# Revit family: 4C-Max_Height_Units_FL.rfa
name_source: partatom
category: Specialty Equipment
revit_build: Autodesk Revit 2016 (Build: 20150714_1515(x64)
units: mm (PartAtom-declared; Revit-internal decimal feet)

## family parameters
Always vertical = Yes
Cut with Voids When Loaded = No
Host = Wall
Part Type = Normal
Room Calculation Point = No
Round Connector Dimension = Use Diameter
Shared = No

## types (12) — shared parameters
Assembly Code = C1030910
Back Enclosure Material = Aluminum - Salsbury Finish = Anodized
Depth = 17.025"
Height = 56.719"
Latch Locks Left Side = No
Latch Locks Right Side = No
Lock Material = Stainless Steel -Salsbury Finish =  Polished
Manufacturer = Salsbury Industries
MasterFormat Number = 10 55 00
MasterFormat Title = Postal Specialties
Version = 2.0 (08/09/16)

## per-type parameters (varying)
- 3716D-20 FL: Bottom Back Plate=Yes; Description=Max Height Unit: 20 MB1, 2 PL4.5, OM2; Door Slot L1=3700 Series 4C Door Configurations : MB1 Door; Door Slot L10=3700 Series 4C Door Configurations : MB1 Door w/ Divider; Door Slot L11=3700 Series 4C Door Configurations : MB1 Door w/ Divider; Door Slot L16=3700 Series 4C Parcel Configurations : PL4.5 w/ Divider; Door Slot L2=3700 Series 4C Door Configurations : MB1 Door w/ Divider; Door Slot L3=3700 Series 4C Door Configurations : MB1 Door w/ Divider; Door Slot L4=3700 Series 4C Door Configurations : MB1 Door w/ Divider; Door Slot L5=3700 Series 4C Door Configurations : MB1 Door w/ Divider; Door Slot L6=3700 Series 4C Door Configurations : MB1 Door w/ Divider; Door Slot L7=3700 Series 4C Door Configurations : MB1 Door w/ Divider; Door Slot L8=3700 Series 4C Door Configurations : MB1 Door w/ Divider; Door Slot L9=3700 Series 4C Door Configurations : MB1 Door w/ Divider; Door Slot R1=3700 Series 4C Door Configurations : MB1 Door; Door Slot R10=3700 Series 4C Door Configurations : MB1 Door w/ Divider; Door Slot R11=3700 Series 4C Door Configurations : MB1 Door w/ Divider; Door Slot R16=3700 Series 4C Parcel Configurations : PL4.5 w/ Divider; Door Slot R2=3700 Series 4C Door Configurations : MB1 Door w/ Divider; Door Slot R3=3700 Series 4C Door Configurations : MB1 Door w/ Divider; Door Slot R4=3700 Series 4C Door Configurations : MB1 Door w/ Divider; Door Slot R5=3700 Series 4C Door Configurations : MB1 Door w/ Divider; Door Slot R6=3700 Series 4C Door Configurations : MB1 Door w/ Divider; Door Slot R7=3700 Series 4C Door Configurations : Empty; Door Slot R8=3700 Series 4C OM2 Configuration : OM2-FL; Door Slot R9=3700 Series 4C Door Configurations : MB1 Door w/ Divider; Latch Alignment=14.857"; Left Inside Wall=Yes; Right Inside Wall=Yes; Top Back Plate=Yes; Type Comments=4C Standard Horizontal Mailbox - Front Loading; Vertical Center Divider=Yes; Width=31.098"
- 3716S-09 FL: Bottom Back Plate=No; Description=Max Height Unit: 9 MB1, 1 PL4.5, OM2; Door Slot L1=3700 Series 4C Door Configurations : Empty; Door Slot L10=3700 Series 4C Door Configurations : Empty; Door Slot L11=3700 Series 4C Door Configurations : Empty; Door Slot L16=3700 Series 4C Door Configurations : Empty; Door Slot L2=3700 Series 4C Door Configurations : Empty; Door Slot L3=3700 Series 4C Door Configurations : Empty; Door Slot L4=3700 Series 4C Door Configurations : Empty; Door Slot L5=3700 Series 4C Door Configurations : Empty; Door Slot L6=3700 Series 4C Door Configurations : Empty; Door Slot L7=3700 Series 4C Door Configurations : Empty; Door Slot L8=3700 Series 4C Door Configurations : Empty; Door Slot L9=3700 Series 4C Door Configurations : Empty; Door Slot R1=3700 Series 4C Door Configurations : MB1 Door; Door Slot R10=3700 Series 4C Door Configurations : MB1 Door w/ Divider; Door Slot R11=3700 Series 4C Door Configurations : MB1 Door w/ Divider; Door Slot R16=3700 Series 4C Parcel Configurations : PL4.5 w/ Divider; Door Slot R2=3700 Series 4C Door Configurations : MB1 Door w/ Divider; Door Slot R3=3700 Series 4C Door Configurations : MB1 Door w/ Divider; Door Slot R4=3700 Series 4C Door Configurations : MB1 Door w/ Divider; Door Slot R5=3700 Series 4C Door Configurations : MB1 Door w/ Divider; Door Slot R6=3700 Series 4C Door Configurations : MB1 Door w/ Divider; Door Slot R7=3700 Series 4C Door Configurations : Empty; Door Slot R8=3700 Series 4C OM2 Configuration : OM2-FL; Door Slot R9=3700 Series 4C Door Configurations : MB1 Door w/ Divider; Latch Alignment=13.876"; Left Inside Wall=No; Right Inside Wall=No; Top Back Plate=No; Type Comments=4C Standard Horizontal Mailbox - Front Loading; Vertical Center Divider=No; Width=16.344"
- 3716S-04 FL: Bottom Back Plate=No; Description=Max Height Unit: 3 MB2, 1 MB3, 1 PL4.5, OM2; Door Slot L1=3700 Series 4C Door Configurations : Empty; Door Slot L10=3700 Series 4C Door Configurations : Empty; Door Slot L11=3700 Series 4C Door Configurations : Empty; Door Slot L16=3700 Series 4C Door Configurations : Empty; Door Slot L2=3700 Series 4C Door Configurations : Empty; Door Slot L3=3700 Series 4C Door Configurations : Empty; Door Slot L4=3700 Series 4C Door Configurations : Empty; Door Slot L5=3700 Series 4C Door Configurations : Empty; Door Slot L6=3700 Series 4C Door Configurations : Empty; Door Slot L7=3700 Series 4C Door Configurations : Empty; Door Slot L8=3700 Series 4C Door Configurations : Empty; Door Slot L9=3700 Series 4C Door Configurations : Empty; Door Slot R1=3700 Series 4C Door Configurations : Empty; Door Slot R10=3700 Series 4C Door Configurations : Empty; Door Slot R11=3700 Series 4C Door Configurations : MB3 Door w/ Divider; Door Slot R16=3700 Series 4C Parcel Configurations : PL4.5 w/ Divider; Door Slot R2=3700 Series 4C Door Configurations : MB2 Door; Door Slot R3=3700 Series 4C Door Configurations : Empty; Door Slot R4=3700 Series 4C Door Configurations : MB2 Door w/ Divider; Door Slot R5=3700 Series 4C Door Configurations : Empty; Door Slot R6=3700 Series 4C Door Configurations : MB2 Door w/ Divider; Door Slot R7=3700 Series 4C Door Configurations : Empty; Door Slot R8=3700 Series 4C OM2 Configuration : OM2-FL; Door Slot R9=3700 Series 4C Door Configurations : Empty; Latch Alignment=13.876"; Left Inside Wall=No; Right Inside Wall=No; Top Back Plate=No; Type Comments=4C Standard Horizontal Mailbox - Front Loading; Vertical Center Divider=No; Width=16.344"
- 3716S-03 FL: Bottom Back Plate=No; Description=Max Height Unit: 3 MB3, 1 PL4.5, OM2; Door Slot L1=3700 Series 4C Door Configurations : Empty; Door Slot L10=3700 Series 4C Door Configurations : Empty; Door Slot L11=3700 Series 4C Door Configurations : Empty; Door Slot L16=3700 Series 4C Door Configurations : Empty; Door Slot L2=3700 Series 4C Door Configurations : Empty; Door Slot L3=3700 Series 4C Door Configurations : Empty; Door Slot L4=3700 Series 4C Door Configurations : Empty; Door Slot L5=3700 Series 4C Door Configurations : Empty; Door Slot L6=3700 Series 4C Door Configurations : Empty; Door Slot L7=3700 Series 4C Door Configurations : Empty; Door Slot L8=3700 Series 4C Door Configurations : Empty; Door Slot L9=3700 Series 4C Door Configurations : Empty; Door Slot R1=3700 Series 4C Door Configurations : Empty; Door Slot R10=3700 Series 4C Door Configurations : Empty; Door Slot R11=3700 Series 4C Door Configurations : MB3 Door w/ Divider; Door Slot R16=3700 Series 4C Parcel Configurations : PL4.5 w/ Divider; Door Slot R2=3700 Series 4C Door Configurations : Empty; Door Slot R3=3700 Series 4C Door Configurations : MB3 Door; Door Slot R4=3700 Series 4C Door Configurations : Empty; Door Slot R5=3700 Series 4C Door Configurations : Empty; Door Slot R6=3700 Series 4C Door Configurations : MB3 Door w/ Divider; Door Slot R7=3700 Series 4C Door Configurations : Empty; Door Slot R8=3700 Series 4C OM2 Configuration : OM2-FL; Door Slot R9=3700 Series 4C Door Configurations : Empty; Latch Alignment=13.876"; Left Inside Wall=No; Right Inside Wall=No; Top Back Plate=No; Type Comments=4C Standard Horizontal Mailbox - Front Loading; Vertical Center Divider=No; Width=16.344"
- 3716S-3P FL: Bottom Back Plate=No; Description=Max Height Unit: 1 PL4.5, 1 PL5, 1 PL6; Door Slot L1=3700 Series 4C Door Configurations : Empty; Door Slot L10=3700 Series 4C Door Configurations : Empty; Door Slot L11=3700 Series 4C Door Configurations : Empty; Door Slot L16=3700 Series 4C Door Configurations : Empty; Door Slot L2=3700 Series 4C Door Configurations : Empty; Door Slot L3=3700 Series 4C Door Configurations : Empty; Door Slot L4=3700 Series 4C Door Configurations : Empty; Door Slot L5=3700 Series 4C Door Configurations : Empty; Door Slot L6=3700 Series 4C Door Configurations : Empty; Door Slot L7=3700 Series 4C Door Configurations : Empty; Door Slot L8=3700 Series 4C Door Configurations : Empty; Door Slot L9=3700 Series 4C Door Configurations : Empty; Door Slot R1=3700 Series 4C Door Configurations : Empty; Door Slot R10=3700 Series 4C Door Configurations : Empty; Door Slot R11=3700 Series 4C Parcel Configurations : PL6 w/ Divider; Door Slot R16=3700 Series 4C Parcel Configurations : PL4.5 w/ Divider; Door Slot R2=3700 Series 4C Door Configurations : Empty; Door Slot R3=3700 Series 4C Door Configurations : Empty; Door Slot R4=3700 Series 4C Door Configurations : Empty; Door Slot R5=3700 Series 4C Parcel Configurations : PL5; Door Slot R6=3700 Series 4C Door Configurations : Empty; Door Slot R7=3700 Series 4C Door Configurations : Empty; Door Slot R8=3700 Series 4C Door Configurations : Empty; Door Slot R9=3700 Series 4C Door Configurations : Empty; Latch Alignment=13.876"; Left Inside Wall=No; Right Inside Wall=No; Top Back Plate=No; Type Comments=4C Standard Horizontal Mailbox - Front Loading; Vertical Center Divider=No; Width=16.344"
- 3716S-2B FL: Bottom Back Plate=No; Description=Maximum Height Unit - 2 Receptacle Bins; Door Slot L1=3700 Series 4C Door Configurations : Empty; Door Slot L10=3700 Series 4C Door Configurations : Empty; Door Slot L11=3700 Series 4C Door Configurations : Empty; Door Slot L16=3700 Series 4C Door Configurations : Empty; Door Slot L2=3700 Series 4C Door Configurations : Empty; Door Slot L3=3700 Series 4C Door Configurations : Empty; Door Slot L4=3700 Series 4C Door Configurations : Empty; Door Slot L5=3700 Series 4C Door Configurations : Empty; Door Slot L6=3700 Series 4C Door Configurations : Empty; Door Slot L7=3700 Series 4C Door Configurations : Empty; Door Slot L8=3700 Series 4C Door Configurations : Empty; Door Slot L9=3700 Series 4C Door Configurations : Empty; Door Slot R1=3700 Series 4C Door Configurations : Empty; Door Slot R10=3700 Series 4C Door Configurations : Empty; Door Slot R11=3700 Series 4C Door Configurations : Empty; Door Slot R16=4C-Max Height Receptacle; Door Slot R2=3700 Series 4C Door Configurations : Empty; Door Slot R3=3700 Series 4C Door Configurations : Empty; Door Slot R4=3700 Series 4C Door Configurations : Empty; Door Slot R5=3700 Series 4C Door Configurations : Empty; Door Slot R6=3700 Series 4C Door Configurations : Empty; Door Slot R7=3700 Series 4C Door Configurations : Empty; Door Slot R8=3700 Series 4C Door Configurations : Empty; Door Slot R9=3700 Series 4C Door Configurations : Empty; Latch Alignment=13.876"; Left Inside Wall=No; Right Inside Wall=No; Top Back Plate=No; Type Comments=4C Horizontal Receptacle Bin - Front Loading; Vertical Center Divider=No; Width=16.344"
- 3716D-19 FL: Bottom Back Plate=Yes; Description=Max Height Unit: 19 MB1, 2 PL4.5, OM3; Door Slot L1=3700 Series 4C Door Configurations : MB1 Door; Door Slot L10=3700 Series 4C Door Configurations : MB1 Door w/ Divider; Door Slot L11=3700 Series 4C Door Configurations : MB1 Door w/ Divider; Door Slot L16=3700 Series 4C Parcel Configurations : PL4.5 w/ Divider; Door Slot L2=3700 Series 4C Door Configurations : MB1 Door w/ Divider; Door Slot L3=3700 Series 4C Door Configurations : MB1 Door w/ Divider; Door Slot L4=3700 Series 4C Door Configurations : MB1 Door w/ Divider; Door Slot L5=3700 Series 4C Door Configurations : MB1 Door w/ Divider; Door Slot L6=3700 Series 4C Door Configurations : MB1 Door w/ Divider; Door Slot L7=3700 Series 4C Door Configurations : MB1 Door w/ Divider; Door Slot L8=3700 Series 4C Door Configurations : MB1 Door w/ Divider; Door Slot L9=3700 Series 4C Door Configurations : MB1 Door w/ Divider; Door Slot R1=3700 Series 4C Door Configurations : MB1 Door; Door Slot R10=3700 Series 4C Door Configurations : MB1 Door w/ Divider; Door Slot R11=3700 Series 4C Door Configurations : MB1 Door w/ Divider; Door Slot R16=3700 Series 4C Parcel Configurations : PL4.5 w/ Divider; Door Slot R2=3700 Series 4C Door Configurations : MB1 Door w/ Divider; Door Slot R3=3700 Series 4C Door Configurations : MB1 Door w/ Divider; Door Slot R4=3700 Series 4C Door Configurations : MB1 Door w/ Divider; Door Slot R5=3700 Series 4C Door Configurations : MB1 Door w/ Divider; Door Slot R6=3700 Series 4C Door Configurations : MB1 Door w/ Divider; Door Slot R7=3700 Series 4C Door Configurations : Empty; Door Slot R8=3700 Series 4C Door Configurations : Empty; Door Slot R9=3700 Series 4C OM3 Configuration : OM3-FL; Latch Alignment=14.857"; Left Inside Wall=Yes; Right Inside Wall=Yes; Top Back Plate=Yes; Type Comments=4C Standard Horizontal Mailbox - Front Loading; Vertical Center Divider=Yes; Width=31.098"
- 3716D-09 FL: Bottom Back Plate=Yes; Description=Max Height Unit: 7 MB2, 2 MB3, 2 PL4.5, OM2; Door Slot L1=3700 Series 4C Door Configurations : Empty; Door Slot L10=3700 Series 4C Door Configurations : Empty; Door Slot L11=3700 Series 4C Door Configurations : MB3 Door w/ Divider; Door Slot L16=3700 Series 4C Parcel Configurations : PL4.5 w/ Divider; Door Slot L2=3700 Series 4C Door Configurations : MB2 Door; Door Slot L3=3700 Series 4C Door Configurations : Empty; Door Slot L4=3700 Series 4C Door Configurations : MB2 Door w/ Divider; Door Slot L5=3700 Series 4C Door Configurations : Empty; Door Slot L6=3700 Series 4C Door Configurations : MB2 Door w/ Divider; Door Slot L7=3700 Series 4C Door Configurations : Empty; Door Slot L8=3700 Series 4C Door Configurations : MB2 Door w/ Divider; Door Slot L9=3700 Series 4C Door Configurations : Empty; Door Slot R1=3700 Series 4C Door Configurations : Empty; Door Slot R10=3700 Series 4C Door Configurations : Empty; Door Slot R11=3700 Series 4C Door Configurations : MB3 Door w/ Divider; Door Slot R16=3700 Series 4C Parcel Configurations : PL4.5 w/ Divider; Door Slot R2=3700 Series 4C Door Configurations : MB2 Door; Door Slot R3=3700 Series 4C Door Configurations : Empty; Door Slot R4=3700 Series 4C Door Configurations : MB2 Door w/ Divider; Door Slot R5=3700 Series 4C Door Configurations : Empty; Door Slot R6=3700 Series 4C Door Configurations : MB2 Door w/ Divider; Door Slot R7=3700 Series 4C Door Configurations : Empty; Door Slot R8=3700 Series 4C OM2 Configuration : OM2-FL; Door Slot R9=3700 Series 4C Door Configurations : Empty; Latch Alignment=14.857"; Left Inside Wall=Yes; Right Inside Wall=Yes; Top Back Plate=Yes; Type Comments=4C Standard Horizontal Mailbox - Front Loading; Vertical Center Divider=Yes; Width=31.098"
- 3716D-07 FL: Bottom Back Plate=Yes; Description=Max Height Unit: 1 MB2, 6 MB3, 2 PL4.5, OM2; Door Slot L1=3700 Series 4C Door Configurations : Empty; Door Slot L10=3700 Series 4C Door Configurations : Empty; Door Slot L11=3700 Series 4C Door Configurations : MB3 Door w/ Divider; Door Slot L16=3700 Series 4C Parcel Configurations : PL4.5 w/ Divider; Door Slot L2=3700 Series 4C Door Configurations : Empty; Door Slot L3=3700 Series 4C Door Configurations : MB3 Door; Door Slot L4=3700 Series 4C Door Configurations : Empty; Door Slot L5=3700 Series 4C Door Configurations : Empty; Door Slot L6=3700 Series 4C Door Configurations : MB3 Door w/ Divider; Door Slot L7=3700 Series 4C Door Configurations : Empty; Door Slot L8=3700 Series 4C Door Configurations : MB2 Door w/ Divider; Door Slot L9=3700 Series 4C Door Configurations : Empty; Door Slot R1=3700 Series 4C Door Configurations : Empty; Door Slot R10=3700 Series 4C Door Configurations : Empty; Door Slot R11=3700 Series 4C Door Configurations : MB3 Door w/ Divider; Door Slot R16=3700 Series 4C Parcel Configurations : PL4.5 w/ Divider; Door Slot R2=3700 Series 4C Door Configurations : Empty; Door Slot R3=3700 Series 4C Door Configurations : MB3 Door; Door Slot R4=3700 Series 4C Door Configurations : Empty; Door Slot R5=3700 Series 4C Door Configurations : Empty; Door Slot R6=3700 Series 4C Door Configurations : MB3 Door w/ Divider; Door Slot R7=3700 Series 4C Door Configurations : Empty; Door Slot R8=3700 Series 4C OM2 Configuration : OM2-FL; Door Slot R9=3700 Series 4C Door Configurations : Empty; Latch Alignment=14.857"; Left Inside Wall=Yes; Right Inside Wall=Yes; Top Back Plate=Yes; Type Comments=4C Standard Horizontal Mailbox - Front Loading; Vertical Center Divider=Yes; Width=31.098"
- 3716D-8P FL: Bottom Back Plate=Yes; Description=Max Height Unit: 4 PL3, 1 PL4, 2 PL4.5, 1 PL5, CA; Door Slot L1=3700 Series 4C Door Configurations : Empty; Door Slot L10=3700 Series 4C Door Configurations : Empty; Door Slot L11=3700 Series 4C Parcel Configurations : PL5 w/ Divider; Door Slot L16=3700 Series 4C Parcel Configurations : PL4.5 w/ Divider; Door Slot L2=3700 Series 4C Door Configurations : Empty; Door Slot L3=3700 Series 4C Parcel Configurations : PL3; Door Slot L4=3700 Series 4C Door Configurations : Empty; Door Slot L5=3700 Series 4C Door Configurations : Empty; Door Slot L6=3700 Series 4C Parcel Configurations : PL3 w/ Divider; Door Slot L7=3700 Series 4C Door Configurations : Empty; Door Slot L8=3700 Series 4C Door Configurations : Empty; Door Slot L9=3700 Series 4C Door Configurations : Empty; Door Slot R1=3700 Series 4C Door Configurations : Empty; Door Slot R10=3700 Series 4C Door Configurations : Empty; Door Slot R11=3700 Series 4C Parcel Configurations : PL3 w/ Divider; Door Slot R16=3700 Series 4C Parcel Configurations : PL4.5 w/ Divider; Door Slot R2=3700 Series 4C Door Configurations : Empty; Door Slot R3=3700 Series 4C Parcel Configurations : PL3; Door Slot R4=3700 Series 4C Door Configurations : Empty; Door Slot R5=3700 Series 4C Door Configurations : Empty; Door Slot R6=3700 Series 4C Door Configurations : Empty; Door Slot R7=3700 Series 4C Parcel Configurations : PL4 w/ Divider; Door Slot R8=3700 Series 4C OM1 Configuration : OM1-FL; Door Slot R9=3700 Series 4C Door Configurations : Empty; Latch Alignment=14.857"; Left Inside Wall=Yes; Right Inside Wall=Yes; Top Back Plate=Yes; Type Comments=4C Standard Horizontal Mailbox - Front Loading; Vertical Center Divider=Yes; Width=31.098"
- 3716D-6P FL: Bottom Back Plate=Yes; Description=Max Height Unit: 1 PL4, 2 PL4.5, 1 PL5, 2 PL6, CA; Door Slot L1=3700 Series 4C Door Configurations : Empty; Door Slot L10=3700 Series 4C Door Configurations : Empty; Door Slot L11=3700 Series 4C Parcel Configurations : PL5 w/ Divider; Door Slot L16=3700 Series 4C Parcel Configurations : PL4.5 w/ Divider; Door Slot L2=3700 Series 4C Door Configurations : Empty; Door Slot L3=3700 Series 4C Door Configurations : Empty; Door Slot L4=3700 Series 4C Door Configurations : Empty; Door Slot L5=3700 Series 4C Door Configurations : Empty; Door Slot L6=3700 Series 4C Parcel Configurations : PL6; Door Slot L7=3700 Series 4C Door Configurations : Empty; Door Slot L8=3700 Series 4C Door Configurations : Empty; Door Slot L9=3700 Series 4C Door Configurations : Empty; Door Slot R1=3700 Series 4C Door Configurations : Empty; Door Slot R10=3700 Series 4C Door Configurations : Empty; Door Slot R11=3700 Series 4C Parcel Configurations : PL4 w/ Divider; Door Slot R16=3700 Series 4C Parcel Configurations : PL4.5 w/ Divider; Door Slot R2=3700 Series 4C Door Configurations : Empty; Door Slot R3=3700 Series 4C Door Configurations : Empty; Door Slot R4=3700 Series 4C Door Configurations : Empty; Door Slot R5=3700 Series 4C Door Configurations : Empty; Door Slot R6=3700 Series 4C Parcel Configurations : PL6; Door Slot R7=3700 Series 4C OM1 Configuration : OM1-FL; Door Slot R8=3700 Series 4C Door Configurations : Empty; Door Slot R9=3700 Series 4C Door Configurations : Empty; Latch Alignment=14.857"; Left Inside Wall=Yes; Right Inside Wall=Yes; Top Back Plate=Yes; Type Comments=4C Standard Horizontal Mailbox - Front Loading; Vertical Center Divider=Yes; Width=31.098"
- 3716S-1C FL: Bottom Back Plate=No; Description=Max Height Unit; Door Slot L1=3700 Series 4C Door Configurations : Empty; Door Slot L10=3700 Series 4C Door Configurations : Empty; Door Slot L11=3700 Series 4C Door Configurations : Empty; Door Slot L16=3700 Series 4C Door Configurations : Empty; Door Slot L2=3700 Series 4C Door Configurations : Empty; Door Slot L3=3700 Series 4C Door Configurations : Empty; Door Slot L4=3700 Series 4C Door Configurations : Empty; Door Slot L5=3700 Series 4C Door Configurations : Empty; Door Slot L6=3700 Series 4C Door Configurations : Empty; Door Slot L7=3700 Series 4C Door Configurations : Empty; Door Slot L8=3700 Series 4C Door Configurations : Empty; Door Slot L9=3700 Series 4C Door Configurations : Empty; Door Slot R1=3700 Series 4C Door Configurations : Empty; Door Slot R10=3700 Series 4C Door Configurations : Empty; Door Slot R11=3700 Series 4C Door Configurations : Empty; Door Slot R16=4C-Max Height Collection Box; Door Slot R2=3700 Series 4C Door Configurations : Empty; Door Slot R3=3700 Series 4C Door Configurations : Empty; Door Slot R4=3700 Series 4C Door Configurations : Empty; Door Slot R5=3700 Series 4C Door Configurations : Empty; Door Slot R6=3700 Series 4C Door Configurations : Empty; Door Slot R7=3700 Series 4C Door Configurations : Empty; Door Slot R8=3700 Series 4C Door Configurations : Empty; Door Slot R9=3700 Series 4C Door Configurations : Empty; Latch Alignment=13.876"; Left Inside Wall=No; Right Inside Wall=No; Top Back Plate=No; Type Comments=4C Horizontal Collection Box - Front Loading; Vertical Center Divider=No; Width=16.344"

note: column(s) folded — value = type name in every type: Model

## geometry (parser evidence)
native form markers: Blend x18, Extrusion x9, Sweep x80
no freeform markers — native parametric forms only
